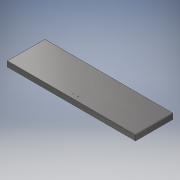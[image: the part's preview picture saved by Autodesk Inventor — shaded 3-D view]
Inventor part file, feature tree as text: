
AUTODESK INVENTOR PART (.ipt)
format: ipt  version: 2017 (Build 210142000, 142)  size: 223,232 bytes
history: native  units: mm
features: sheet_metal_op x7, other x6, sketch x4, reference x2, extrude x1
ambient origin geometry x8: Origin, YZ Plane, XZ Plane, XY Plane, X Axis, Y Axis, Z Axis, Center Point
bodies: Solid1 (feature_tree)
feature tree (20):
  sheet_metal_op  "Face1"
  sheet_metal_op  "Flange1"
  sheet_metal_op  "Flange2"
  extrude  "Extrusion1"  Depth=278.299mm
  sketch  "Sketch1"  dims[d0=936.598mm d1=278.299mm]
  other  "Plate1"
  sketch  "Sketch2"  dims[d2=1.5mm]
  other  "Plate2"
  sheet_metal_op  "Bend1"
  sheet_metal_op  "Corner1"
  sketch  "Sketch3"  dims[d3=1.5mm]
  other  "Plate3"
  sheet_metal_op  "Bend2"
  sheet_metal_op  "Corner2"
  sketch  "Sketch4"  dims[d4=0.75mm d5=3.0mm d6=1.5mm d7=40.0mm d8=90.0deg d9=1.5mm d10=6.0mm d11=1.5mm d12=1.5mm d13=1.5mm d14=0.75mm d15=3.0mm d16=1.5mm d17=10.0mm d18=90.0deg d19=1.5mm d20=6.0mm d21=1.5mm d22=1.5mm d23=10.0mm d24=0.0mm]
  reference  "Reference1"
  reference  "Reference2"
  other  "Definition1"
  other  "Bancada de Lavagem Mãos - 1150 x 370 x 900h.iam"
  other  "Batente batoque Inferior:1"
